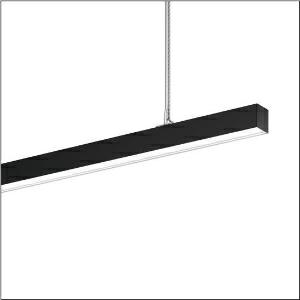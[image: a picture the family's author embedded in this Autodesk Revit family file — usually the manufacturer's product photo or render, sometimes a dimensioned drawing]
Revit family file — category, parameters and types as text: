
# Revit family: silica_r__21_51mx30tct9b_d278
name_source: partatom
category: Lighting Fixtures
units: mm (PartAtom-declared; Revit-internal decimal feet)

## family parameters
Cut with Voids When Loaded = No
Host = Face
Light Source = No
Part Type = Normal
Room Calculation Point = No
Round Connector Dimension = Use Diameter
Shared = No

## types (1)
- --- (1 x LED, 10300 lm, 84.4 W, 6500K)
    Apparent Load = 84 VA
    CIE Flux Codes = 47 79 96 58 100
    Color Rendering = 80
    Color Temperature = 6500K
    Default Elevation = 1800 mm
    Description = Silica® 21, office luminaire, primary optical cover: cover, of PMMA, opal, light emission: direct/indirect distribution, primary light characteristic: symmetric, installation type: suspended mounting, LED, rated luminous flux: 10.300lm, luminous efficacy: 116lm/W, light colour: 8tw, colour temperature: 2700..6500K, control gear: ECG DALI, with terminal, 3+2-pole, max. 2.5mm², mains connection: 220..240V, AC, 50/60Hz, rated input power: 88.7W, luminaire housing, of aluminium, jet black (RAL 9005), length: 3.004mm, width: 53mm, height: 53mm, protection rating (complete): IP20, insulation class (complete): insulation class I (protective earthing), certification: CE, permissible operating ambient temperature: 0..+35°C, standard: EN 50419, packaging unit: 1 piece
    Height = 53 mm
    Lamp = 1 x LED
    Lamp Light Flux = 10300 lm
    Lamp Power = 84.4 W
    Lamp count = 1
    Length = 3004 mm
    Luminous efficacy = 122 lm/W
    Manufacturer = Siteco
    ModVariant = No
    Model = 51MX30TCT9B
    Mounting Place = Ceiling
    Mounting Type = Pendant
    Number of Poles = 1
    OnlyDefault = Yes
    Power Factor = 1
    Product Name = Silica® 21
    Product group = office luminaire | ceiling pendant
    ProductGroupID = 902
    Protection Class = Protection class I
    Protection Degree = IP 20
    RLX_Detail_Level = 1
    RLX_Emergency_Light_Flux = 0 lm
    RLX_Emergency_Type = 0
    RLX_Emergency_Type_DB = No
    RlxData = <blob elided: 22761 chars, md5=7c0a7c6d>
    Socket = socket
    Standby Power = 0 W
    System Light Flux = 10300 lm
    System Power = 84 W
    Type Comments = individual setting
    Type Image = l_1297744.jpg
    URL = http://relux.com
    VarID = @adj_070951
    Voltage = 0 V
    Weight = 0.00 kg
    Width = 53 mm

## geometry (parser evidence)
native form markers: Blend x4, Sweep x14
no freeform markers — native parametric forms only
